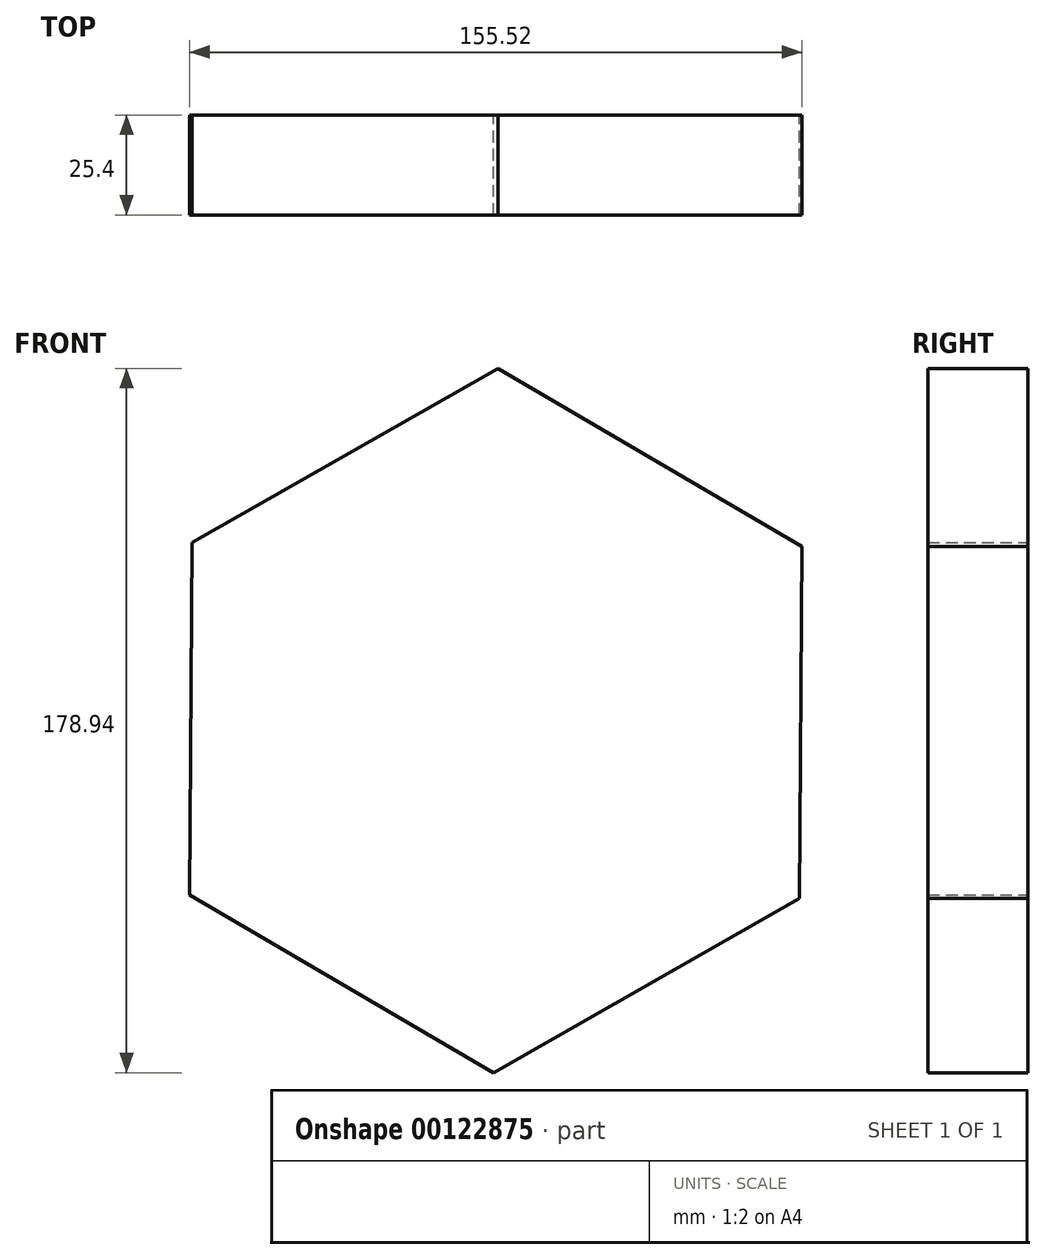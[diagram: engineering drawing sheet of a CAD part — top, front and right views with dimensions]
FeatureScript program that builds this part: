
annotation { "Feature Type Name" : "Feature", "Feature Type Description" : "" }
export const myFeature = defineFeature(function(context is Context, id is Id, definition is map)
    precondition{}
    {
        {
            var Q0;
            Q0=qCreatedBy(makeId("Front.planeOp"),FACE);
            var sketch = newSketch(context, id + "F0", { "sketchPlane" : qUnion([Q0])});
            skCircle(sketch, "E0.cCircle", {"center": v(0, 0) * mm, "radius": 77.48 * mm, "construction": true});
            skLineSegment(sketch, "E0.0", {"start": v(77.2, -45.21) * mm, "end": v(-0.55, -89.47) * mm});
            skLineSegment(sketch, "E0.1", {"start": v(-0.55, -89.47) * mm, "end": v(-77.76, -44.25) * mm});
            skLineSegment(sketch, "E0.2", {"start": v(-77.76, -44.25) * mm, "end": v(-77.2, 45.21) * mm});
            skLineSegment(sketch, "E0.3", {"start": v(-77.2, 45.21) * mm, "end": v(0.55, 89.47) * mm});
            skLineSegment(sketch, "E0.4", {"start": v(0.55, 89.47) * mm, "end": v(77.76, 44.25) * mm});
            skLineSegment(sketch, "E0.5", {"start": v(77.76, 44.25) * mm, "end": v(77.2, -45.21) * mm});
            skPoint(sketch, "E0.0.midPoint", {"position": v(38.33, -67.34) * mm});
            skSolve(sketch);
        }
        {
            var Q0;
            Q0=makeQuery(id+"F0.imprint","IMPRINT",FACE,{"disambiguationData":[TD([[makeQuery(id+"F0.imprint","IMPRINT",EDGE,{"derivedFrom":sQuery(id+"F0.wireOp",EDGE,"E0.0")}),-1.0]])]});
            extrude(context, id + "F1", {"entities" : qUnion([Q0]), "depth" : 25.4 * mm});
        }
    });
